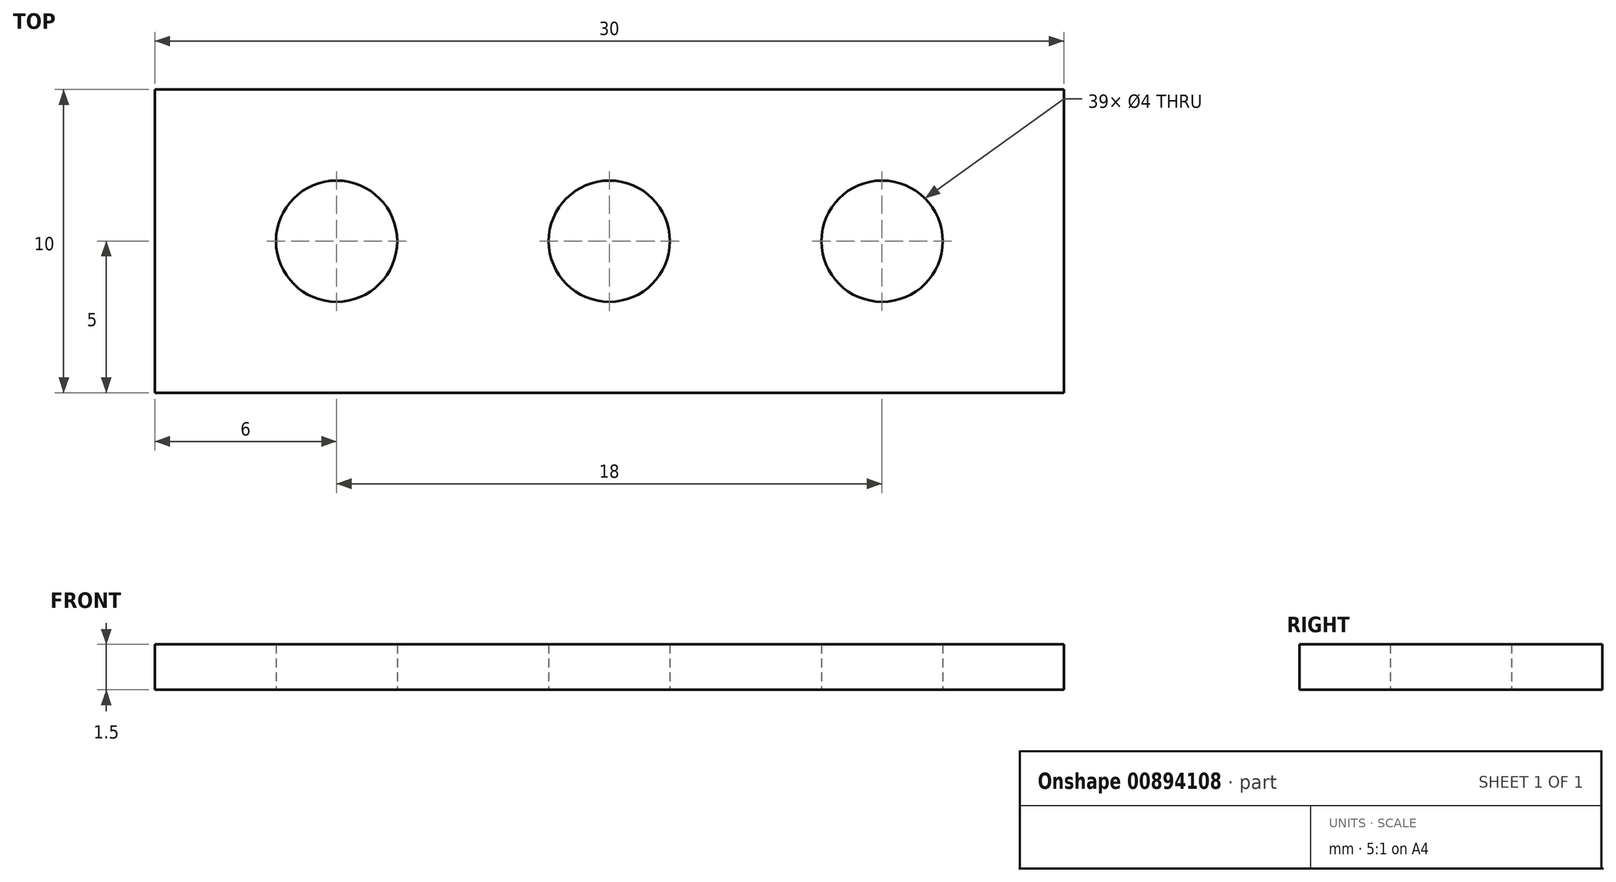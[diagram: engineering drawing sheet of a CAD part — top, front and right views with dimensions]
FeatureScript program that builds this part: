
annotation { "Feature Type Name" : "Feature", "Feature Type Description" : "" }
export const myFeature = defineFeature(function(context is Context, id is Id, definition is map)
    precondition{}
    {
        {
            var Q0;
            Q0=qCreatedBy(makeId("Top.planeOp"),FACE);
            var sketch = newSketch(context, id + "F0", { "sketchPlane" : qUnion([Q0])});
            skLineSegment(sketch, "E0.bottom", {"start": v(15, -5) * mm, "end": v(-15, -5) * mm});
            skLineSegment(sketch, "E0.top", {"start": v(15, 5) * mm, "end": v(-15, 5) * mm});
            skLineSegment(sketch, "E0.left", {"start": v(15, -5) * mm, "end": v(15, 5) * mm});
            skLineSegment(sketch, "E0.right", {"start": v(-15, -5) * mm, "end": v(-15, 5) * mm});
            skPoint(sketch, "E0.middle", {"position": v(0, 0) * mm});
            skCircle(sketch, "E1", {"center": v(0, 0) * mm, "radius": 2 * mm});
            skCircle(sketch, "E2", {"center": v(9, 0) * mm, "radius": 2 * mm});
            skCircle(sketch, "E3", {"center": v(-9, 0) * mm, "radius": 2 * mm});
            skLineSegment(sketch, "E4", {"start": v(-5, 5) * mm, "end": v(-5, -5) * mm});
            skLineSegment(sketch, "E5", {"start": v(5, 5) * mm, "end": v(5, -5) * mm});
            skSolve(sketch);
        }
        {
            var Q0;
            {var subQ0=sQuery(id+"F0.wireOp",EDGE,"E0.right");Q0=makeQuery(id+"F0.imprint","IMPRINT",FACE,{"disambiguationData":[TD([[makeQuery(id+"F0.imprint","IMPRINT",EDGE,{"derivedFrom":subQ0}),-1.0]])]});}
            var Q1;
            {var subQ0=sQuery(id+"F0.wireOp",EDGE,"E0.left");Q1=makeQuery(id+"F0.imprint","IMPRINT",FACE,{"disambiguationData":[TD([[makeQuery(id+"F0.imprint","IMPRINT",EDGE,{"derivedFrom":subQ0}),1.0]])]});}
            var Q2;
            Q2=makeQuery(id+"F0.imprint","IMPRINT",FACE,{"disambiguationData":[TD([[makeQuery(id+"F0.imprint","IMPRINT",EDGE,{"derivedFrom":sQuery(id+"F0.wireOp",EDGE,"E1")}),-1.0]])]});
            extrude(context, id + "F1", {"entities" : qUnion([Q0, Q1, Q2]), "depth" : 1.5 * mm, "offsetDistance" : 25 * mm});
        }
    });
